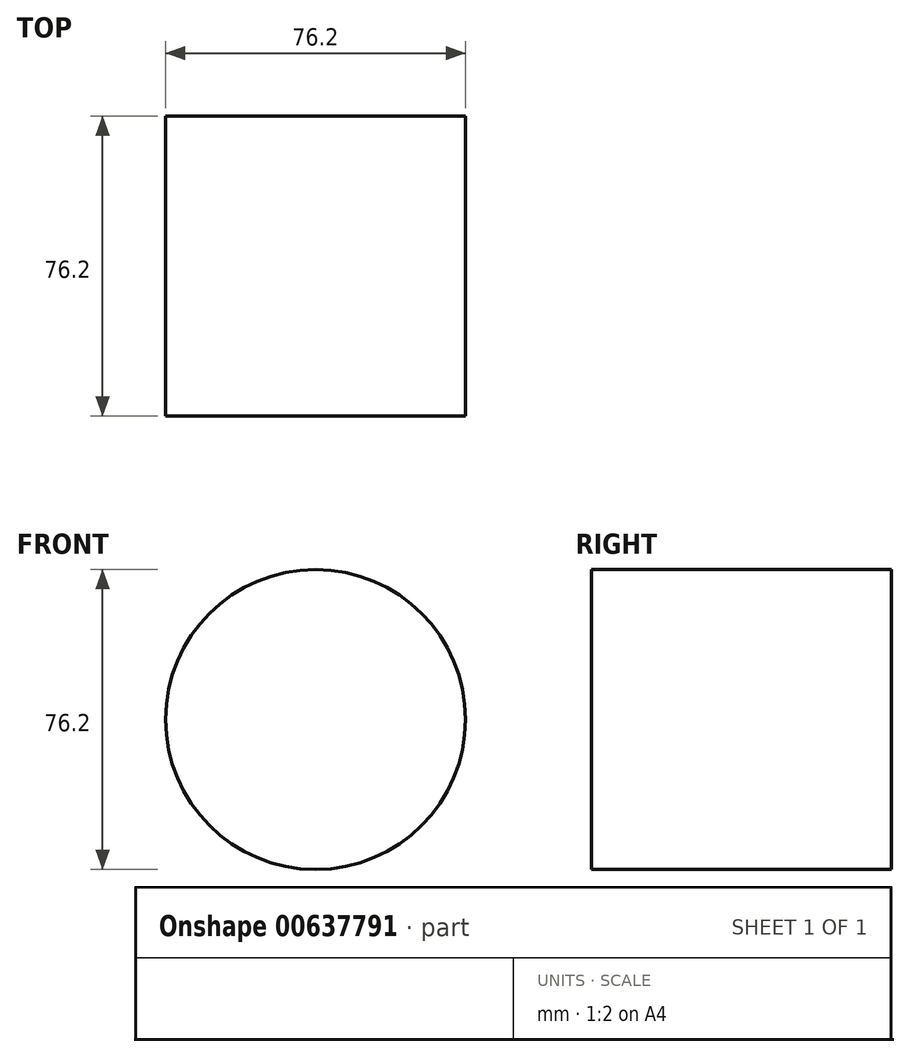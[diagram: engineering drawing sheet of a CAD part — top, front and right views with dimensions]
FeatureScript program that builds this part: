
annotation { "Feature Type Name" : "Feature", "Feature Type Description" : "" }
export const myFeature = defineFeature(function(context is Context, id is Id, definition is map)
    precondition{}
    {
        {
            var Q0;
            Q0=qCreatedBy(makeId("Front.planeOp"),FACE);
            var sketch = newSketch(context, id + "F0", { "sketchPlane" : qUnion([Q0])});
            skCircle(sketch, "E0", {"center": v(0, 0) * mm, "radius": 38.1 * mm});
            skSolve(sketch);
        }
        {
            var Q0;
            Q0 = qSketchRegion(id + "F0", true);
            extrude(context, id + "F1", {"entities" : qUnion([Q0]), "depth" : 76.2 * mm, "offsetDistance" : 25.4 * mm});
        }
    });
